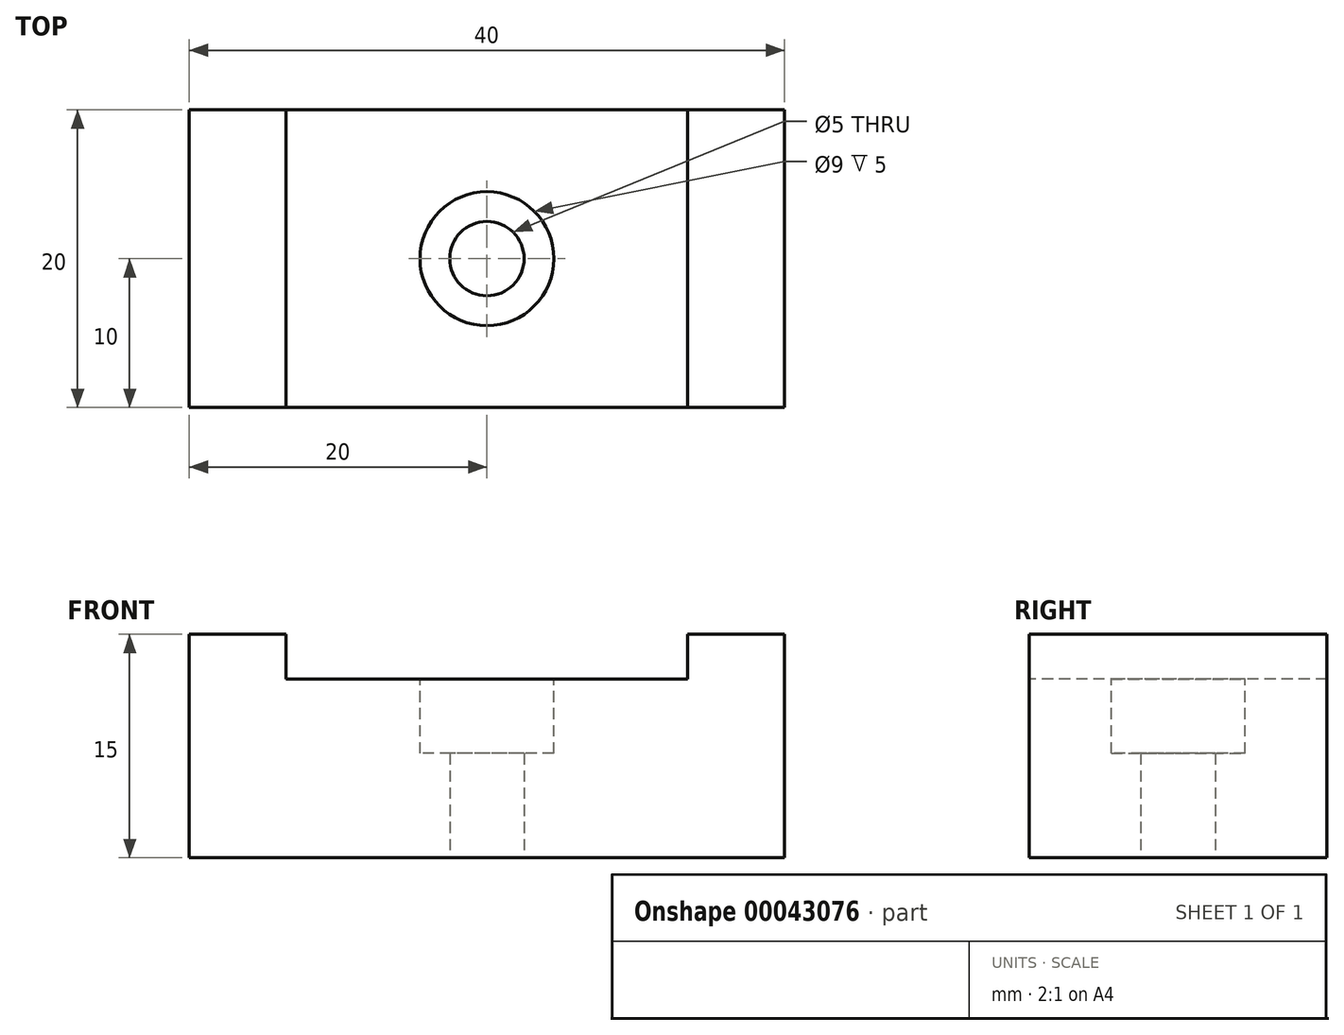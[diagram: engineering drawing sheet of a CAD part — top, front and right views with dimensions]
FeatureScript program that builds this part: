
annotation { "Feature Type Name" : "Feature", "Feature Type Description" : "" }
export const myFeature = defineFeature(function(context is Context, id is Id, definition is map)
    precondition{}
    {
        {
            var Q0;
            Q0=qCreatedBy(makeId("Top.planeOp"),FACE);
            var sketch = newSketch(context, id + "F0", { "sketchPlane" : qUnion([Q0])});
            skLineSegment(sketch, "E0.bottom", {"start": v(-20, 10) * mm, "end": v(20, 10) * mm});
            skLineSegment(sketch, "E0.top", {"start": v(-20, -10) * mm, "end": v(20, -10) * mm});
            skLineSegment(sketch, "E0.left", {"start": v(-20, 10) * mm, "end": v(-20, -10) * mm});
            skLineSegment(sketch, "E0.right", {"start": v(20, 10) * mm, "end": v(20, -10) * mm});
            skLineSegment(sketch, "E1", {"start": v(0, 63.08) * mm, "end": v(0, -43.08) * mm, "construction": true});
            skPoint(sketch, "E2", {"position": v(0, 10) * mm});
            skPoint(sketch, "E3", {"position": v(20, 0) * mm});
            skLineSegment(sketch, "E4", {"start": v(-70.3, 0) * mm, "end": v(110.3, 0) * mm, "construction": true});
            skCircle(sketch, "E5", {"center": v(0, 0) * mm, "radius": 2.5 * mm});
            skSolve(sketch);
        }
        {
            var Q0;
            Q0=makeQuery(id+"F0.imprint","IMPRINT",FACE,{"disambiguationData":[TD([[makeQuery(id+"F0.imprint","IMPRINT",EDGE,{"derivedFrom":sQuery(id+"F0.wireOp",EDGE,"E0.bottom")}),-1.0]])]});
            extrude(context, id + "F1", {"entities" : qUnion([Q0]), "depth" : 15 * mm});
        }
        {
            var Q0;
            Q0=makeQuery(id+"F1.opExtrude","CAP_FACE",FACE,{"disambiguationData":[OSD([sQuery(id+"F0.wireOp",EDGE,"E0.bottom"),sQuery(id+"F0.wireOp",EDGE,"E0.top"),sQuery(id+"F0.wireOp",EDGE,"E0.left"),sQuery(id+"F0.wireOp",EDGE,"E0.right"),sQuery(id+"F0.wireOp",EDGE,"E5")])],"isStart":false});
            var sketch = newSketch(context, id + "F2", { "sketchPlane" : qUnion([Q0])});
            skLineSegment(sketch, "E6.rect.bottom", {"start": v(13.5, 10) * mm, "end": v(-13.5, 10) * mm});
            skLineSegment(sketch, "E6.rect.top", {"start": v(13.5, -10) * mm, "end": v(-13.5, -10) * mm});
            skLineSegment(sketch, "E6.rect.left", {"start": v(13.5, 10) * mm, "end": v(13.5, -10) * mm});
            skLineSegment(sketch, "E6.rect.right", {"start": v(-13.5, 10) * mm, "end": v(-13.5, -10) * mm});
            skPoint(sketch, "E6.rect.middle", {"position": v(0, 0) * mm});
            skSolve(sketch);
        }
        {
            var Q0;
            Q0=makeQuery(id+"F2.imprint","IMPRINT",FACE,{"disambiguationData":[TD([[makeQuery(id+"F2.imprint","IMPRINT",EDGE,{"derivedFrom":sQuery(id+"F2.wireOp",EDGE,"E6.rect.bottom")}),-1.0]])]});
            extrude(context, id + "F3", {"entities" : qUnion([Q0]), "operationType" : NewBodyOperationType.REMOVE, "oppositeDirection" : true, "depth" : 3 * mm});
        }
        {
            var Q0;
            Q0=makeQuery(id+"F3.boolean.opBoolean","COPY",FACE,{"derivedFrom":makeQuery(id+"F3.opExtrude","CAP_FACE",FACE,{"disambiguationData":[OSD([sQuery(id+"F0.wireOp",EDGE,"E5"),sQuery(id+"F2.wireOp",EDGE,"E6.rect.bottom"),sQuery(id+"F2.wireOp",EDGE,"E6.rect.top"),sQuery(id+"F2.wireOp",EDGE,"E6.rect.left"),sQuery(id+"F2.wireOp",EDGE,"E6.rect.right")])],"isStart":false})});
            var sketch = newSketch(context, id + "F4", { "sketchPlane" : qUnion([Q0])});
            skCircle(sketch, "E7", {"center": v(0, 0) * mm, "radius": 4.5 * mm});
            skSolve(sketch);
        }
        {
            var Q0;
            Q0=makeQuery(id+"F4.imprint","IMPRINT",FACE,{"disambiguationData":[TD([[makeQuery(id+"F4.imprint","IMPRINT",EDGE,{"derivedFrom":sQuery(id+"F4.wireOp",EDGE,"E7")}),1.0]])]});
            extrude(context, id + "F5", {"entities" : qUnion([Q0]), "operationType" : NewBodyOperationType.REMOVE, "oppositeDirection" : true, "depth" : 5 * mm});
        }
    });
